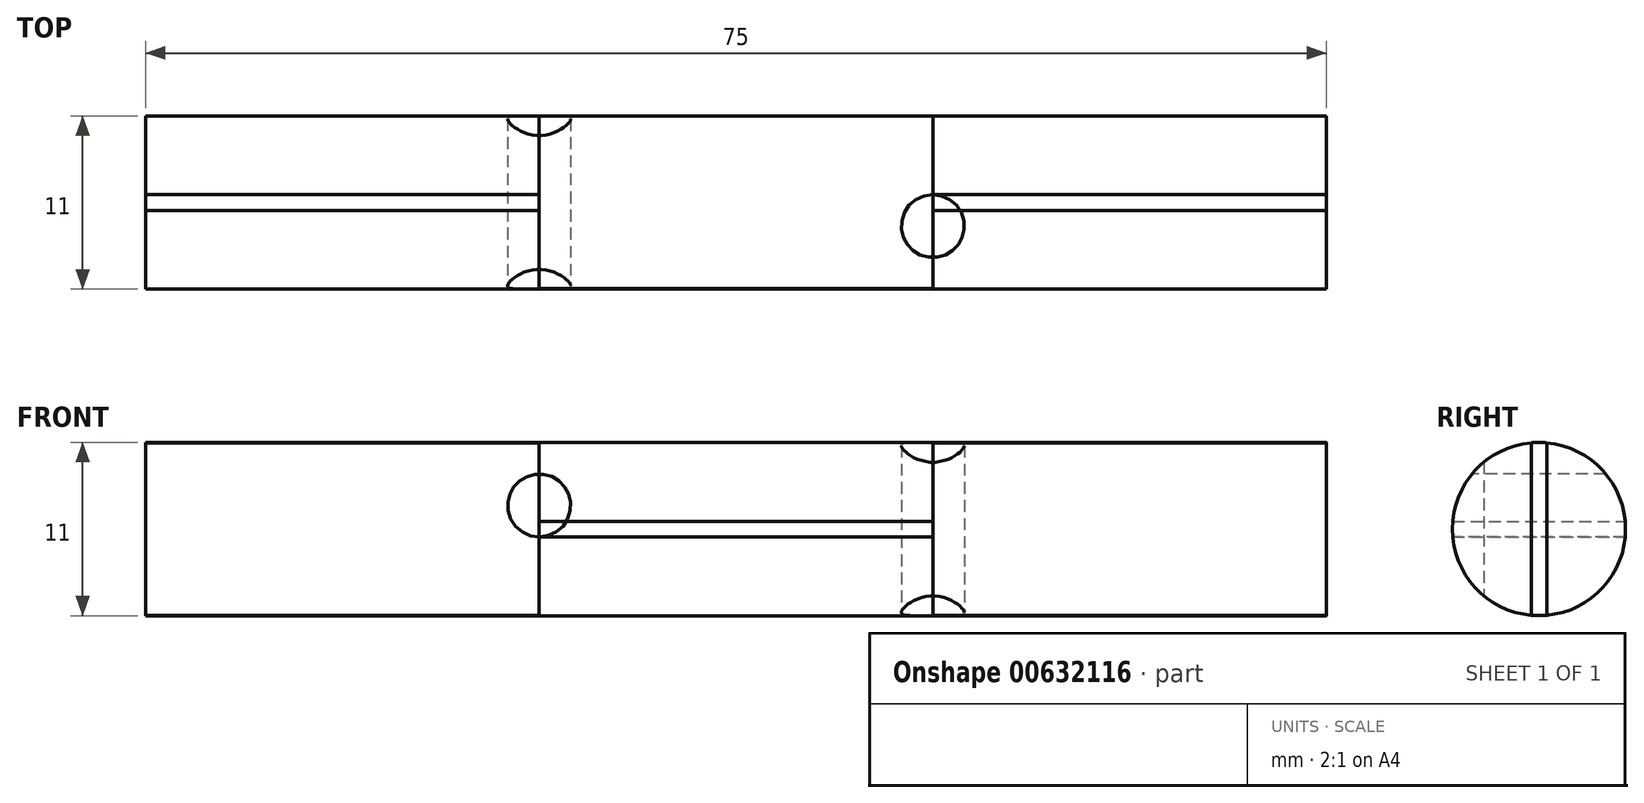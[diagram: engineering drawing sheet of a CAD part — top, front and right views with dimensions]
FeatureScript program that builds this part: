
annotation { "Feature Type Name" : "Feature", "Feature Type Description" : "" }
export const myFeature = defineFeature(function(context is Context, id is Id, definition is map)
    precondition{}
    {
        {
            var Q0;
            Q0=qCreatedBy(makeId("Top.planeOp"),FACE);
            var sketch = newSketch(context, id + "F0", { "sketchPlane" : qUnion([Q0])});
            skLineSegment(sketch, "E0", {"start": v(0, 0) * mm, "end": v(0, 10) * mm});
            skLineSegment(sketch, "E1", {"start": v(0, 10) * mm, "end": v(100, 10) * mm});
            skLineSegment(sketch, "E2", {"start": v(100, 10) * mm, "end": v(100, -10) * mm});
            skLineSegment(sketch, "E3", {"start": v(100, -10) * mm, "end": v(0, -10) * mm});
            skLineSegment(sketch, "E4", {"start": v(0, -10) * mm, "end": v(0, 0) * mm});
            skLineSegment(sketch, "E5", {"start": v(0, 0.5) * mm, "end": v(100, 0.5) * mm});
            skLineSegment(sketch, "E6", {"start": v(0, -0.5) * mm, "end": v(100, -0.5) * mm});
            skLineSegment(sketch, "E7", {"start": v(25, 10) * mm, "end": v(25, -10) * mm});
            skLineSegment(sketch, "E8", {"start": v(50, 10) * mm, "end": v(50, -10) * mm});
            skLineSegment(sketch, "E9", {"start": v(75, 10) * mm, "end": v(75, -10) * mm});
            skSolve(sketch);
        }
        {
            var Q0;
            {var subQ0=sQuery(id+"F0.wireOp",EDGE,"E4");var subQ1=sQuery(id+"F0.wireOp",EDGE,"E3");var subQ2=makeQuery(id+"F0.imprint","INTERSECT",VERTEX,{"derivedFrom":[subQ1,subQ0]});Q0=makeQuery(id+"F0.imprint","IMPRINT",FACE,{"disambiguationData":[TD([[makeQuery(id+"F0.imprint","IMPRINT",EDGE,{"disambiguationData":[TD([[subQ2,1.0]])],"derivedFrom":subQ1}),-1.0]])]});}
            var Q1;
            {var subQ0=sQuery(id+"F0.wireOp",EDGE,"E1");var subQ1=sQuery(id+"F0.wireOp",EDGE,"E0");var subQ2=makeQuery(id+"F0.imprint","INTERSECT",VERTEX,{"derivedFrom":[subQ1,subQ0]});Q1=makeQuery(id+"F0.imprint","IMPRINT",FACE,{"disambiguationData":[TD([[makeQuery(id+"F0.imprint","IMPRINT",EDGE,{"disambiguationData":[TD([[subQ2,1.0]])],"derivedFrom":subQ1}),-1.0]])]});}
            extrude(context, id + "F1", {"entities" : qUnion([Q0, Q1]), "endBound" : BoundingType.SYMMETRIC, "depth" : 20 * mm, "offsetDistance" : 25 * mm});
        }
        {
            var Q0;
            {var subQ1=sQuery(id+"F0.wireOp",EDGE,"E4");var subQ5=sQuery(id+"F0.wireOp",EDGE,"E0");var subQ6=makeQuery(id+"F0.imprint","INTERSECT",VERTEX,{"derivedFrom":[subQ5,subQ1]});Q0=makeQuery(id+"F0.imprint","IMPRINT",FACE,{"disambiguationData":[TD([[makeQuery(id+"F0.imprint","IMPRINT",EDGE,{"disambiguationData":[TD([[subQ6,-1.0]])],"derivedFrom":subQ5}),-1.0]])]});}
            extrude(context, id + "F2", {"entities" : qUnion([Q0]), "endBound" : BoundingType.SYMMETRIC, "depth" : 20 * mm, "offsetDistance" : 25 * mm});
        }
        {
            var Q0;
            Q0=makeQuery(id+"F1.opExtrude","SWEPT_BODY",BODY,{"disambiguationData":[OSD([sQuery(id+"F0.wireOp",EDGE,"E3"),sQuery(id+"F0.wireOp",EDGE,"E4"),sQuery(id+"F0.wireOp",EDGE,"E6"),sQuery(id+"F0.wireOp",EDGE,"E7")])]});
            var Q1;
            Q1=makeQuery(id+"F1.opExtrude","SWEPT_BODY",BODY,{"disambiguationData":[OSD([sQuery(id+"F0.wireOp",EDGE,"E0"),sQuery(id+"F0.wireOp",EDGE,"E1"),sQuery(id+"F0.wireOp",EDGE,"E5"),sQuery(id+"F0.wireOp",EDGE,"E7")])]});
            var Q2;
            Q2=makeQuery(id+"F2.opExtrude","SWEPT_BODY",BODY,{"disambiguationData":[OSD([sQuery(id+"F0.wireOp",EDGE,"E0"),sQuery(id+"F0.wireOp",EDGE,"E4"),sQuery(id+"F0.wireOp",EDGE,"E5"),sQuery(id+"F0.wireOp",EDGE,"E6"),sQuery(id+"F0.wireOp",EDGE,"E7")])]});
            var Q3;
            Q3=makeQuery(id+"F1.opExtrude","CAP_EDGE",EDGE,{"disambiguationData":[OSD([sQuery(id+"F0.wireOp",EDGE,"E1")])],"isStart":false});
            transform(context, id + "F3", {"entities" : qUnion([Q0, Q1, Q2]), "transformType" : TransformType.TRANSLATION_DISTANCE, "transformDirection" : qUnion([Q3]), "distance" : 25 * mm, "makeCopy" : true});
        }
        {
            var Q0;
            Q0=qCreatedBy(makeId("Front.planeOp"),FACE);
            var sketch = newSketch(context, id + "F4", { "sketchPlane" : qUnion([Q0])});
            skLineSegment(sketch, "E10.bottom", {"start": v(0, 4) * mm, "end": v(73.56, 4) * mm});
            skLineSegment(sketch, "E11", {"start": v(0, 0) * mm, "end": v(73.56, 0) * mm, "construction": true});
            skLineSegment(sketch, "E12", {"start": v(0, 4) * mm, "end": v(0, 0) * mm});
            skLineSegment(sketch, "E13", {"start": v(73.56, 0) * mm, "end": v(73.56, 4) * mm});
            skLineSegment(sketch, "E14", {"start": v(0, 0) * mm, "end": v(73.56, 0) * mm});
            skSolve(sketch);
        }
        {
            var Q0;
            Q0=makeQuery(id+"F3.opPattern","COPY",BODY,{"derivedFrom":makeQuery(id+"F1.opExtrude","SWEPT_BODY",BODY,{"disambiguationData":[OSD([sQuery(id+"F0.wireOp",EDGE,"E0"),sQuery(id+"F0.wireOp",EDGE,"E1"),sQuery(id+"F0.wireOp",EDGE,"E5"),sQuery(id+"F0.wireOp",EDGE,"E7")])]}),"instanceName":"1"});
            var Q1;
            Q1=makeQuery(id+"F3.opPattern","COPY",BODY,{"derivedFrom":makeQuery(id+"F2.opExtrude","SWEPT_BODY",BODY,{"disambiguationData":[OSD([sQuery(id+"F0.wireOp",EDGE,"E0"),sQuery(id+"F0.wireOp",EDGE,"E4"),sQuery(id+"F0.wireOp",EDGE,"E5"),sQuery(id+"F0.wireOp",EDGE,"E6"),sQuery(id+"F0.wireOp",EDGE,"E7")])]}),"instanceName":"1"});
            var Q2;
            Q2=makeQuery(id+"F3.opPattern","COPY",BODY,{"derivedFrom":makeQuery(id+"F1.opExtrude","SWEPT_BODY",BODY,{"disambiguationData":[OSD([sQuery(id+"F0.wireOp",EDGE,"E3"),sQuery(id+"F0.wireOp",EDGE,"E4"),sQuery(id+"F0.wireOp",EDGE,"E6"),sQuery(id+"F0.wireOp",EDGE,"E7")])]}),"instanceName":"1"});
            var Q3;
            Q3=sQuery(id+"F4.wireOp",EDGE,"E14");
            transform(context, id + "F5", {"entities" : qUnion([Q0, Q1, Q2]), "transformType" : TransformType.ROTATION, "transformAxis" : qUnion([Q3]), "angle" : 90 * degree, "makeCopy" : false});
        }
        {
            var Q0;
            Q0=makeQuery(id+"F3.opPattern","COPY",FACE,{"derivedFrom":makeQuery(id+"F1.opExtrude","CAP_FACE",FACE,{"disambiguationData":[OSD([sQuery(id+"F0.wireOp",EDGE,"E3"),sQuery(id+"F0.wireOp",EDGE,"E4"),sQuery(id+"F0.wireOp",EDGE,"E6"),sQuery(id+"F0.wireOp",EDGE,"E7")])],"isStart":false}),"instanceName":"1"});
            var sketch = newSketch(context, id + "F6", { "sketchPlane" : qUnion([Q0])});
            skCircle(sketch, "E15", {"center": v(25, 1.5) * mm, "radius": 2 * mm});
            skSolve(sketch);
        }
        {
            var Q0;
            Q0 = qSketchRegion(id + "F6", true);
            extrude(context, id + "F7", {"entities" : qUnion([Q0]), "oppositeDirection" : true, "depth" : 20 * mm, "offsetDistance" : 25 * mm});
        }
        {
            var Q0;
            Q0=makeQuery(id+"F3.opPattern","COPY",BODY,{"derivedFrom":makeQuery(id+"F1.opExtrude","SWEPT_BODY",BODY,{"disambiguationData":[OSD([sQuery(id+"F0.wireOp",EDGE,"E0"),sQuery(id+"F0.wireOp",EDGE,"E1"),sQuery(id+"F0.wireOp",EDGE,"E5"),sQuery(id+"F0.wireOp",EDGE,"E7")])]}),"instanceName":"1"});
            var Q1;
            Q1=makeQuery(id+"F3.opPattern","COPY",BODY,{"derivedFrom":makeQuery(id+"F2.opExtrude","SWEPT_BODY",BODY,{"disambiguationData":[OSD([sQuery(id+"F0.wireOp",EDGE,"E0"),sQuery(id+"F0.wireOp",EDGE,"E4"),sQuery(id+"F0.wireOp",EDGE,"E5"),sQuery(id+"F0.wireOp",EDGE,"E6"),sQuery(id+"F0.wireOp",EDGE,"E7")])]}),"instanceName":"1"});
            var Q2;
            Q2=makeQuery(id+"F3.opPattern","COPY",BODY,{"derivedFrom":makeQuery(id+"F1.opExtrude","SWEPT_BODY",BODY,{"disambiguationData":[OSD([sQuery(id+"F0.wireOp",EDGE,"E3"),sQuery(id+"F0.wireOp",EDGE,"E4"),sQuery(id+"F0.wireOp",EDGE,"E6"),sQuery(id+"F0.wireOp",EDGE,"E7")])]}),"instanceName":"1"});
            var Q3;
            Q3=makeQuery(id+"F7.opExtrude","SWEPT_BODY",BODY,{"disambiguationData":[OSD([sQuery(id+"F6.wireOp",EDGE,"E15")])]});
            var Q4;
            Q4=makeQuery(id+"F3.opPattern","COPY",EDGE,{"derivedFrom":makeQuery(id+"F1.opExtrude","CAP_EDGE",EDGE,{"disambiguationData":[OSD([sQuery(id+"F0.wireOp",EDGE,"E1")])],"isStart":false}),"instanceName":"1"});
            transform(context, id + "F8", {"entities" : qUnion([Q0, Q1, Q2, Q3]), "transformType" : TransformType.TRANSLATION_DISTANCE, "transformDirection" : qUnion([Q4]), "distance" : 25 * mm, "makeCopy" : true});
        }
        {
            var Q0;
            Q0=makeQuery(id+"F8.opPattern","COPY",BODY,{"derivedFrom":makeQuery(id+"F7.opExtrude","SWEPT_BODY",BODY,{"disambiguationData":[OSD([sQuery(id+"F6.wireOp",EDGE,"E15")])]}),"instanceName":"1"});
            var Q1;
            Q1=makeQuery(id+"F8.opPattern","COPY",BODY,{"derivedFrom":makeQuery(id+"F3.opPattern","COPY",BODY,{"derivedFrom":makeQuery(id+"F1.opExtrude","SWEPT_BODY",BODY,{"disambiguationData":[OSD([sQuery(id+"F0.wireOp",EDGE,"E0"),sQuery(id+"F0.wireOp",EDGE,"E1"),sQuery(id+"F0.wireOp",EDGE,"E5"),sQuery(id+"F0.wireOp",EDGE,"E7")])]}),"instanceName":"1"}),"instanceName":"1"});
            var Q2;
            Q2=makeQuery(id+"F8.opPattern","COPY",BODY,{"derivedFrom":makeQuery(id+"F3.opPattern","COPY",BODY,{"derivedFrom":makeQuery(id+"F2.opExtrude","SWEPT_BODY",BODY,{"disambiguationData":[OSD([sQuery(id+"F0.wireOp",EDGE,"E0"),sQuery(id+"F0.wireOp",EDGE,"E4"),sQuery(id+"F0.wireOp",EDGE,"E5"),sQuery(id+"F0.wireOp",EDGE,"E6"),sQuery(id+"F0.wireOp",EDGE,"E7")])]}),"instanceName":"1"}),"instanceName":"1"});
            var Q3;
            Q3=makeQuery(id+"F8.opPattern","COPY",BODY,{"derivedFrom":makeQuery(id+"F3.opPattern","COPY",BODY,{"derivedFrom":makeQuery(id+"F1.opExtrude","SWEPT_BODY",BODY,{"disambiguationData":[OSD([sQuery(id+"F0.wireOp",EDGE,"E3"),sQuery(id+"F0.wireOp",EDGE,"E4"),sQuery(id+"F0.wireOp",EDGE,"E6"),sQuery(id+"F0.wireOp",EDGE,"E7")])]}),"instanceName":"1"}),"instanceName":"1"});
            var Q4;
            Q4=sQuery(id+"F4.wireOp",EDGE,"E14");
            transform(context, id + "F9", {"entities" : qUnion([Q0, Q1, Q2, Q3]), "transformType" : TransformType.ROTATION, "transformAxis" : qUnion([Q4]), "angle" : 90 * degree, "makeCopy" : false});
        }
        {
            var Q0;
            Q0=qCreatedBy(makeId("Front.planeOp"),FACE);
            var sketch = newSketch(context, id + "F10", { "sketchPlane" : qUnion([Q0])});
            skLineSegment(sketch, "E16.bottom", {"start": v(0, 0) * mm, "end": v(77, 0) * mm});
            skLineSegment(sketch, "E16.top", {"start": v(0, 5.5) * mm, "end": v(77, 5.5) * mm});
            skLineSegment(sketch, "E16.left", {"start": v(0, 0) * mm, "end": v(0, 5.5) * mm});
            skLineSegment(sketch, "E16.right", {"start": v(77, 0) * mm, "end": v(77, 5.5) * mm});
            skSolve(sketch);
        }
        {
            var Q0;
            Q0 = qSketchRegion(id + "F10", true);
            var Q1;
            Q1=sQuery(id+"F4.wireOp",EDGE,"E14");
            revolve(context, id + "F11", {"operationType" : NewBodyOperationType.INTERSECT, "surfaceOperationType" : NewSurfaceOperationType.NEW, "entities" : qUnion([Q0]), "axis" : qUnion([Q1]), "revolveType" : RevolveType.FULL});
        }
    });
